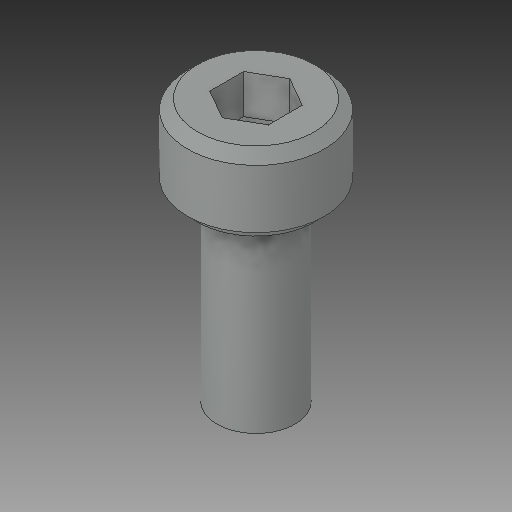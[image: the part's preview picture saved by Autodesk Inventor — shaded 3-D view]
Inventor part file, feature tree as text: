
AUTODESK INVENTOR PART (.ipt)
format: ipt  version: 2017 (Build 210142000, 142)  size: 109,056 bytes
history: native  units: in
note: dims shown in document units (in); Inventor stores cm internally (conversion verified against a paired STEP export)
features: chamfer x1
ambient origin geometry x8: Origin, YZ Plane, XZ Plane, XY Plane, X Axis, Y Axis, Z Axis, Center Point
bodies: Solid1 (feature_tree)
feature tree (1):
  chamfer  "Chamfer2"  [1 undecoded]
note: 1 required parameter value undecoded (feature->parameter linkage not recoverable at this tier; creation-order binding heuristic only, values carry confidence <= 0.55)
